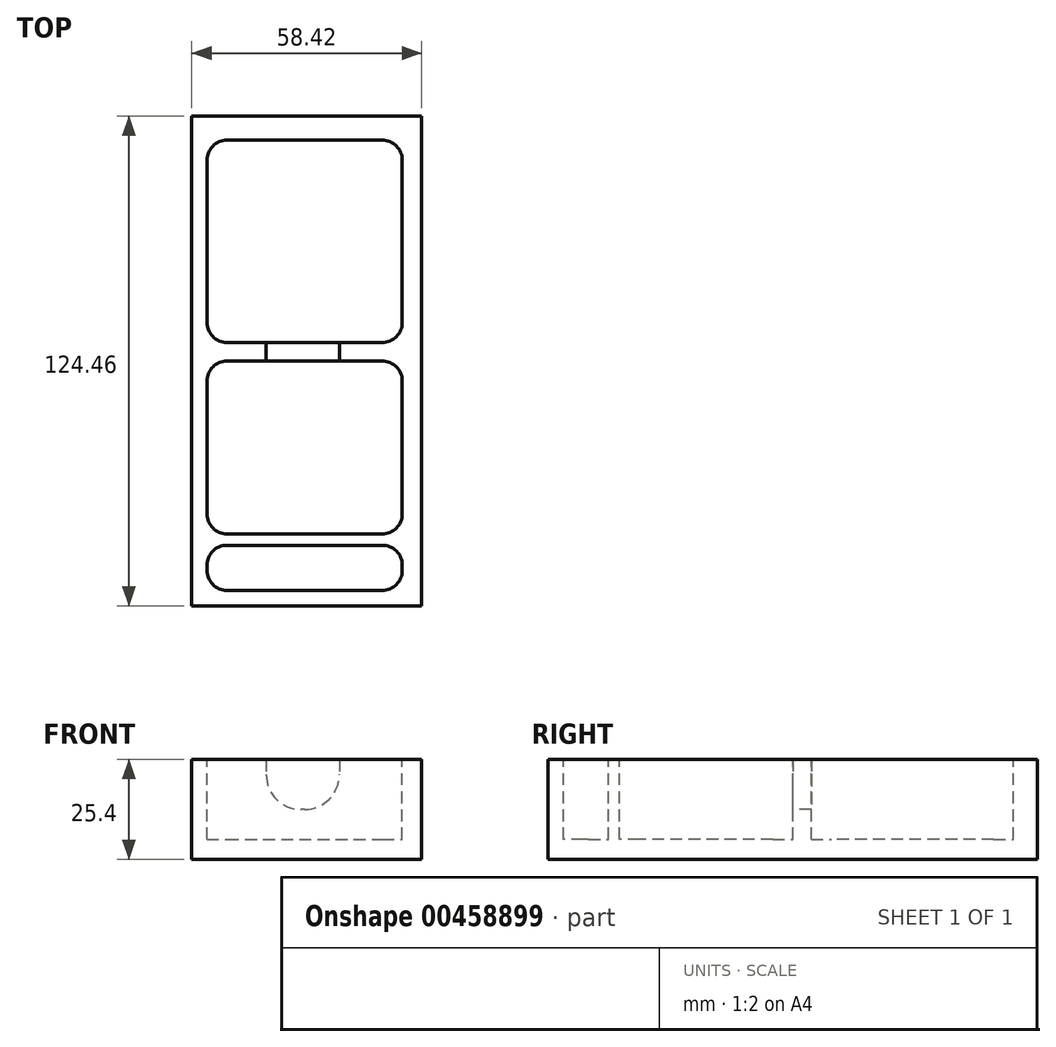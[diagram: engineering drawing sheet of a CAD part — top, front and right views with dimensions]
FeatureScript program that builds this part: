
annotation { "Feature Type Name" : "Feature", "Feature Type Description" : "" }
export const myFeature = defineFeature(function(context is Context, id is Id, definition is map)
    precondition{}
    {
        {
            var Q0;
            Q0=qCreatedBy(makeId("Top.planeOp"),FACE);
            var sketch = newSketch(context, id + "F0", { "sketchPlane" : qUnion([Q0])});
            skLineSegment(sketch, "E0.bottom", {"start": v(-47.75, 64.85) * mm, "end": v(10.67, 64.85) * mm});
            skLineSegment(sketch, "E0.top", {"start": v(-47.75, -59.6) * mm, "end": v(10.67, -59.6) * mm});
            skLineSegment(sketch, "E0.left", {"start": v(-47.75, 64.85) * mm, "end": v(-47.75, -59.6) * mm});
            skLineSegment(sketch, "E0.right", {"start": v(10.67, 64.85) * mm, "end": v(10.67, -59.6) * mm});
            skSolve(sketch);
        }
        {
            var Q0;
            Q0=qSketchRegion(id+"F0",true);
            extrude(context, id + "F1", {"entities" : qUnion([Q0]), "depth" : 25.4 * mm, "offsetDistance" : 25.4 * mm});
        }
        {
            var Q0;
            Q0=makeQuery(id+"F1.opExtrude","CAP_FACE",FACE,{"disambiguationData":[OSD([sQuery(id+"F0.wireOp",EDGE,"E0.bottom"),sQuery(id+"F0.wireOp",EDGE,"E0.top"),sQuery(id+"F0.wireOp",EDGE,"E0.left"),sQuery(id+"F0.wireOp",EDGE,"E0.right")])],"isStart":false});
            var sketch = newSketch(context, id + "F2", { "sketchPlane" : qUnion([Q0])});
            skLineSegment(sketch, "E1.bottom", {"start": v(-43.9, 58.74) * mm, "end": v(5.7, 58.74) * mm});
            skLineSegment(sketch, "E1.top", {"start": v(-43.9, 7.33) * mm, "end": v(5.7, 7.33) * mm});
            skLineSegment(sketch, "E1.left", {"start": v(-43.9, 58.74) * mm, "end": v(-43.9, 7.33) * mm});
            skLineSegment(sketch, "E1.right", {"start": v(5.7, 58.74) * mm, "end": v(5.7, 7.33) * mm});
            skPoint(sketch, "E2.firstSnap0", {"position": v(10.67, 2.62) * mm});
            skLineSegment(sketch, "E2.bottom", {"start": v(-43.9, 2.62) * mm, "end": v(5.7, 2.62) * mm});
            skLineSegment(sketch, "E2.top", {"start": v(-43.9, -41.32) * mm, "end": v(5.7, -41.32) * mm});
            skLineSegment(sketch, "E2.left", {"start": v(-43.9, 2.62) * mm, "end": v(-43.9, -41.32) * mm});
            skLineSegment(sketch, "E2.right", {"start": v(5.7, 2.62) * mm, "end": v(5.7, -41.32) * mm});
            skLineSegment(sketch, "E3.bottom", {"start": v(-43.9, -44.18) * mm, "end": v(5.7, -44.18) * mm});
            skLineSegment(sketch, "E3.top", {"start": v(-43.9, -55.66) * mm, "end": v(5.7, -55.66) * mm});
            skLineSegment(sketch, "E3.left", {"start": v(-43.9, -44.18) * mm, "end": v(-43.9, -55.66) * mm});
            skLineSegment(sketch, "E3.right", {"start": v(5.7, -44.18) * mm, "end": v(5.7, -55.66) * mm});
            skSolve(sketch);
        }
        {
            var Q0;
            Q0 = qSketchRegion(id + "F2", true);
            extrude(context, id + "F3", {"entities" : qUnion([Q0]), "operationType" : NewBodyOperationType.REMOVE, "oppositeDirection" : true, "depth" : 20.32 * mm, "offsetDistance" : 25.4 * mm});
        }
        {
            var Q0;
            Q0=makeQuery(id+"F3.boolean.opBoolean","COPY",EDGE,{"derivedFrom":makeQuery(id+"F3.opExtrude","SWEPT_EDGE",EDGE,{"disambiguationData":[OSD([sQuery(id+"F2.wireOp",EDGE,"E1.bottom"),sQuery(id+"F2.wireOp",EDGE,"E1.right")])]})});
            var Q1;
            Q1=makeQuery(id+"F3.boolean.opBoolean","COPY",EDGE,{"derivedFrom":makeQuery(id+"F3.opExtrude","SWEPT_EDGE",EDGE,{"disambiguationData":[OSD([sQuery(id+"F2.wireOp",EDGE,"E1.bottom"),sQuery(id+"F2.wireOp",EDGE,"E1.left")])]})});
            var Q2;
            Q2=makeQuery(id+"F3.boolean.opBoolean","COPY",EDGE,{"derivedFrom":makeQuery(id+"F3.opExtrude","SWEPT_EDGE",EDGE,{"disambiguationData":[OSD([sQuery(id+"F2.wireOp",EDGE,"E1.top"),sQuery(id+"F2.wireOp",EDGE,"E1.left")])]})});
            var Q3;
            Q3=makeQuery(id+"F3.boolean.opBoolean","COPY",EDGE,{"derivedFrom":makeQuery(id+"F3.opExtrude","SWEPT_EDGE",EDGE,{"disambiguationData":[OSD([sQuery(id+"F2.wireOp",EDGE,"E1.top"),sQuery(id+"F2.wireOp",EDGE,"E1.right")])]})});
            var Q4;
            Q4=makeQuery(id+"F3.boolean.opBoolean","COPY",EDGE,{"derivedFrom":makeQuery(id+"F3.opExtrude","SWEPT_EDGE",EDGE,{"disambiguationData":[OSD([sQuery(id+"F2.wireOp",EDGE,"E2.bottom"),sQuery(id+"F2.wireOp",EDGE,"E2.left")])]})});
            var Q5;
            Q5=makeQuery(id+"F3.boolean.opBoolean","COPY",EDGE,{"derivedFrom":makeQuery(id+"F3.opExtrude","SWEPT_EDGE",EDGE,{"disambiguationData":[OSD([sQuery(id+"F2.wireOp",EDGE,"E2.bottom"),sQuery(id+"F2.wireOp",EDGE,"E2.right")])]})});
            var Q6;
            Q6=makeQuery(id+"F3.boolean.opBoolean","COPY",EDGE,{"derivedFrom":makeQuery(id+"F3.opExtrude","SWEPT_EDGE",EDGE,{"disambiguationData":[OSD([sQuery(id+"F2.wireOp",EDGE,"E2.top"),sQuery(id+"F2.wireOp",EDGE,"E2.right")])]})});
            var Q7;
            Q7=makeQuery(id+"F3.boolean.opBoolean","COPY",EDGE,{"derivedFrom":makeQuery(id+"F3.opExtrude","SWEPT_EDGE",EDGE,{"disambiguationData":[OSD([sQuery(id+"F2.wireOp",EDGE,"E2.top"),sQuery(id+"F2.wireOp",EDGE,"E2.left")])]})});
            var Q8;
            Q8=makeQuery(id+"F3.boolean.opBoolean","COPY",EDGE,{"derivedFrom":makeQuery(id+"F3.opExtrude","SWEPT_EDGE",EDGE,{"disambiguationData":[OSD([sQuery(id+"F2.wireOp",EDGE,"E3.bottom"),sQuery(id+"F2.wireOp",EDGE,"E3.right")])]})});
            var Q9;
            Q9=makeQuery(id+"F3.boolean.opBoolean","COPY",EDGE,{"derivedFrom":makeQuery(id+"F3.opExtrude","SWEPT_EDGE",EDGE,{"disambiguationData":[OSD([sQuery(id+"F2.wireOp",EDGE,"E3.top"),sQuery(id+"F2.wireOp",EDGE,"E3.right")])]})});
            var Q10;
            Q10=makeQuery(id+"F3.boolean.opBoolean","COPY",EDGE,{"derivedFrom":makeQuery(id+"F3.opExtrude","SWEPT_EDGE",EDGE,{"disambiguationData":[OSD([sQuery(id+"F2.wireOp",EDGE,"E3.bottom"),sQuery(id+"F2.wireOp",EDGE,"E3.left")])]})});
            var Q11;
            Q11=makeQuery(id+"F3.boolean.opBoolean","COPY",EDGE,{"derivedFrom":makeQuery(id+"F3.opExtrude","SWEPT_EDGE",EDGE,{"disambiguationData":[OSD([sQuery(id+"F2.wireOp",EDGE,"E3.top"),sQuery(id+"F2.wireOp",EDGE,"E3.left")])]})});
            fillet(context, id + "F4", {"entities" : qUnion([Q0, Q1, Q2, Q3, Q4, Q5, Q6, Q7, Q8, Q9, Q10, Q11]), "radius" : 5.08 * mm, "tangentPropagation" : true, "allowEdgeOverflow" : false});
        }
        {
            var Q0;
            Q0=makeQuery(id+"F1.opExtrude","CAP_FACE",FACE,{"disambiguationData":[OSD([sQuery(id+"F0.wireOp",EDGE,"E0.bottom"),sQuery(id+"F0.wireOp",EDGE,"E0.top"),sQuery(id+"F0.wireOp",EDGE,"E0.left"),sQuery(id+"F0.wireOp",EDGE,"E0.right")])],"isStart":false});
            var sketch = newSketch(context, id + "F5", { "sketchPlane" : qUnion([Q0])});
            skLineSegment(sketch, "E4.bottom", {"start": v(-28.86, 13.22) * mm, "end": v(-10.23, 13.22) * mm});
            skLineSegment(sketch, "E4.top", {"start": v(-28.86, -33.21) * mm, "end": v(-10.23, -33.21) * mm});
            skLineSegment(sketch, "E4.left", {"start": v(-28.86, 13.22) * mm, "end": v(-28.86, -33.21) * mm});
            skLineSegment(sketch, "E4.right", {"start": v(-10.23, 13.22) * mm, "end": v(-10.23, -33.21) * mm});
            skSolve(sketch);
        }
        {
            var Q0;
            Q0 = qSketchRegion(id + "F5", true);
            extrude(context, id + "F6", {"entities" : qUnion([Q0]), "operationType" : NewBodyOperationType.REMOVE, "oppositeDirection" : true, "depth" : 12.7 * mm, "offsetDistance" : 25.4 * mm});
        }
        {
            var Q0;
            {var subQ0=sQuery(id+"F5.wireOp",EDGE,"E4.right");Q0=makeQuery(id+"F6.boolean.opBoolean","COPY",EDGE,{"disambiguationData":[TD([makeQuery(id+"F3.boolean.opBoolean","COPY",FACE,{"derivedFrom":makeQuery(id+"F3.opExtrude","SWEPT_FACE",FACE,{"disambiguationData":[OSD([sQuery(id+"F2.wireOp",EDGE,"E1.top")])]})})])],"derivedFrom":makeQuery(id+"F6.opExtrude","CAP_EDGE",EDGE,{"disambiguationData":[OSD([subQ0])],"isStart":false})});}
            var Q1;
            {var subQ0=sQuery(id+"F5.wireOp",EDGE,"E4.right");Q1=makeQuery(id+"F6.boolean.opBoolean","COPY",EDGE,{"disambiguationData":[TD([makeQuery(id+"F3.boolean.opBoolean","COPY",FACE,{"derivedFrom":makeQuery(id+"F3.opExtrude","SWEPT_FACE",FACE,{"disambiguationData":[OSD([sQuery(id+"F2.wireOp",EDGE,"E2.top")])]})})])],"derivedFrom":makeQuery(id+"F6.opExtrude","CAP_EDGE",EDGE,{"disambiguationData":[OSD([subQ0])],"isStart":false})});}
            var Q2;
            {var subQ0=sQuery(id+"F5.wireOp",EDGE,"E4.left");Q2=makeQuery(id+"F6.boolean.opBoolean","COPY",EDGE,{"disambiguationData":[TD([makeQuery(id+"F3.boolean.opBoolean","COPY",FACE,{"derivedFrom":makeQuery(id+"F3.opExtrude","SWEPT_FACE",FACE,{"disambiguationData":[OSD([sQuery(id+"F2.wireOp",EDGE,"E2.top")])]})})])],"derivedFrom":makeQuery(id+"F6.opExtrude","CAP_EDGE",EDGE,{"disambiguationData":[OSD([subQ0])],"isStart":false})});}
            var Q3;
            {var subQ0=sQuery(id+"F5.wireOp",EDGE,"E4.left");Q3=makeQuery(id+"F6.boolean.opBoolean","COPY",EDGE,{"disambiguationData":[TD([makeQuery(id+"F3.boolean.opBoolean","COPY",FACE,{"derivedFrom":makeQuery(id+"F3.opExtrude","SWEPT_FACE",FACE,{"disambiguationData":[OSD([sQuery(id+"F2.wireOp",EDGE,"E1.top")])]})})])],"derivedFrom":makeQuery(id+"F6.opExtrude","CAP_EDGE",EDGE,{"disambiguationData":[OSD([subQ0])],"isStart":false})});}
            fillet(context, id + "F7", {"entities" : qUnion([Q0, Q1, Q2, Q3]), "radius" : 8.9 * mm, "tangentPropagation" : true, "allowEdgeOverflow" : false});
        }
    });
